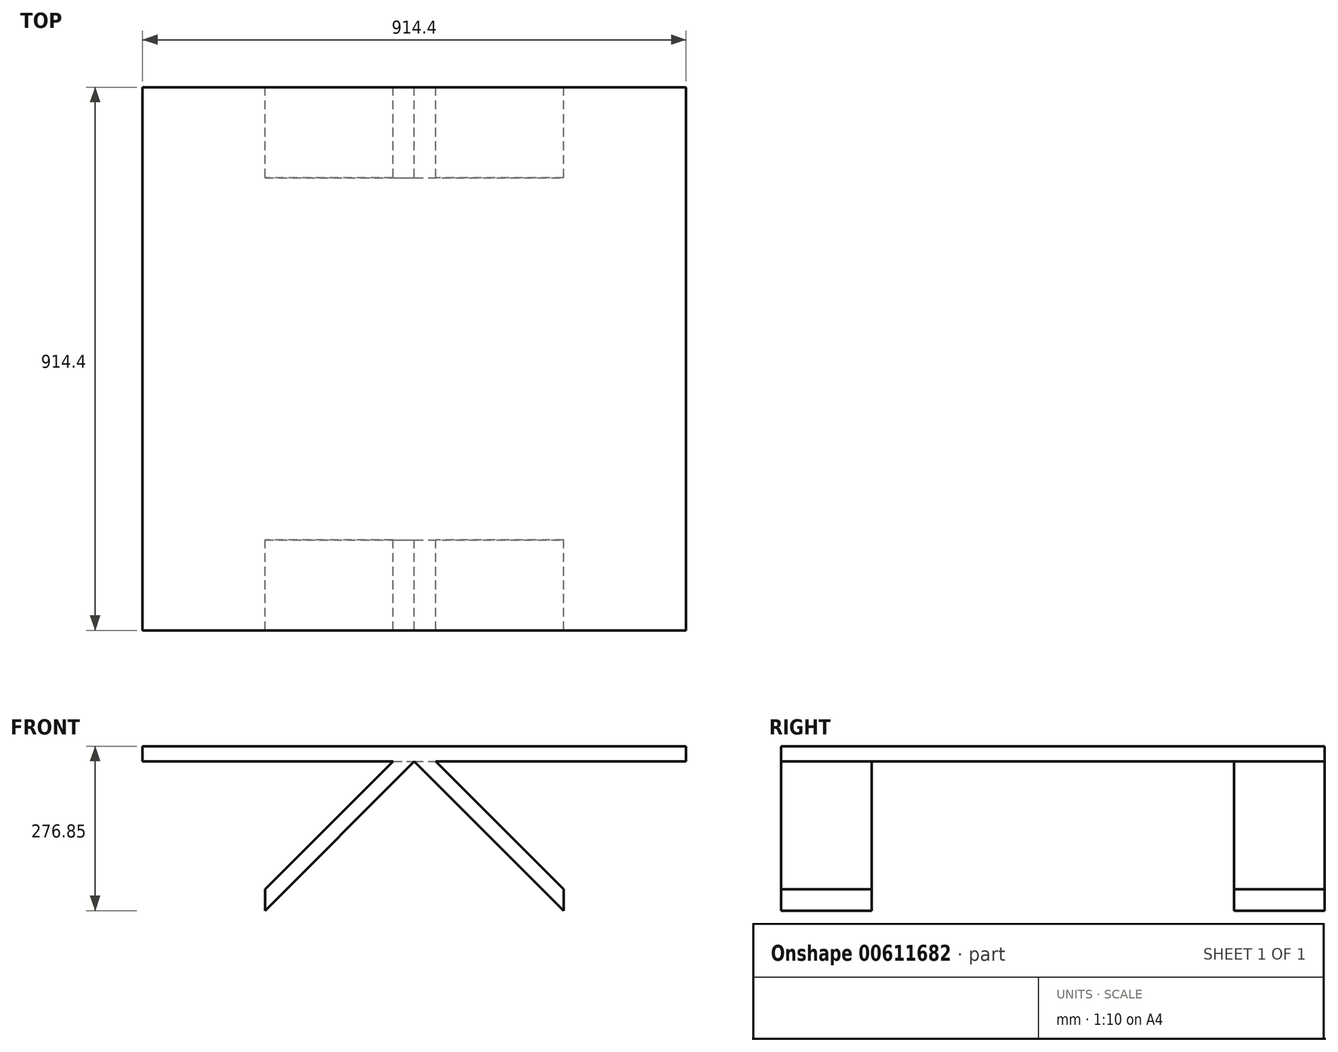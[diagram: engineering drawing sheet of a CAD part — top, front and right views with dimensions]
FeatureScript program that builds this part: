
annotation { "Feature Type Name" : "Feature", "Feature Type Description" : "" }
export const myFeature = defineFeature(function(context is Context, id is Id, definition is map)
    precondition{}
    {
        {
            var Q0;
            Q0=qCreatedBy(makeId("Front.planeOp"),FACE);
            var sketch = newSketch(context, id + "F0", { "sketchPlane" : qUnion([Q0])});
            skLineSegment(sketch, "E0", {"start": v(457.2, 0) * mm, "end": v(-457.2, 0) * mm});
            skLineSegment(sketch, "E1", {"start": v(-457.2, 0) * mm, "end": v(-457.2, 25.4) * mm});
            skLineSegment(sketch, "E2", {"start": v(-457.2, 25.4) * mm, "end": v(457.2, 25.4) * mm});
            skLineSegment(sketch, "E3", {"start": v(457.2, 25.4) * mm, "end": v(457.2, 0) * mm});
            skSolve(sketch);
        }
        {
            var Q0;
            Q0=qCreatedBy(makeId("Front.planeOp"),FACE);
            var sketch = newSketch(context, id + "F1", { "sketchPlane" : qUnion([Q0])});
            skLineSegment(sketch, "E4", {"start": v(-35.92, 0) * mm, "end": v(-251.45, -215.53) * mm});
            skLineSegment(sketch, "E5", {"start": v(-251.45, -215.53) * mm, "end": v(-251.45, -251.45) * mm});
            skLineSegment(sketch, "E6", {"start": v(-251.45, -251.45) * mm, "end": v(0, 0) * mm});
            skLineSegment(sketch, "E7", {"start": v(0, 0) * mm, "end": v(251.45, -251.45) * mm});
            skLineSegment(sketch, "E8", {"start": v(251.45, -251.45) * mm, "end": v(251.45, -215.53) * mm});
            skLineSegment(sketch, "E9", {"start": v(251.45, -215.53) * mm, "end": v(35.92, 0) * mm});
            skPoint(sketch, "E10.start.orphan", {"position": v(-150.22, 0) * mm});
            skPoint(sketch, "E11.end.orphan", {"position": v(152.4, 0) * mm});
            skPoint(sketch, "E11.start.orphan", {"position": v(150.22, -25.4) * mm});
            skLineSegment(sketch, "E12", {"start": v(-35.92, 0) * mm, "end": v(35.92, 0) * mm});
            skSolve(sketch);
        }
        {
            var Q0;
            Q0=makeQuery(id+"F0.imprint","IMPRINT",FACE,{"disambiguationData":[TD([[makeQuery(id+"F0.imprint","IMPRINT",EDGE,{"derivedFrom":sQuery(id+"F0.wireOp",EDGE,"E0")}),-1.0]])]});
            extrude(context, id + "F2", {"entities" : qUnion([Q0]), "endBound" : BoundingType.SYMMETRIC, "depth" : 914.4 * mm, "offsetDistance" : 25.4 * mm});
        }
        {
            var Q0;
            {var subQ0=sQuery(id+"F1.wireOp",EDGE,"E4");Q0=makeQuery(id+"F1.imprint","IMPRINT",FACE,{"disambiguationData":[TD([[makeQuery(id+"F1.imprint","IMPRINT",EDGE,{"derivedFrom":subQ0}),1.0]])]});}
            var Q1;
            {var subQ0=sQuery(id+"F1.wireOp",EDGE,"E7");Q1=makeQuery(id+"F1.imprint","IMPRINT",FACE,{"disambiguationData":[TD([[makeQuery(id+"F1.imprint","IMPRINT",EDGE,{"derivedFrom":subQ0}),1.0]])]});}
            extrude(context, id + "F3", {"entities" : qUnion([Q0, Q1]), "operationType" : NewBodyOperationType.ADD, "endBound" : BoundingType.SYMMETRIC, "depth" : 914.4 * mm, "offsetDistance" : 25.4 * mm});
        }
        {
            var Q0;
            Q0=qCreatedBy(makeId("Front.planeOp"),FACE);
            var sketch = newSketch(context, id + "F4", { "sketchPlane" : qUnion([Q0])});
            skLineSegment(sketch, "E13", {"start": v(-35.92, 0) * mm, "end": v(-251.45, -215.53) * mm});
            skLineSegment(sketch, "E14", {"start": v(-251.45, -215.53) * mm, "end": v(-251.45, -251.45) * mm});
            skLineSegment(sketch, "E15", {"start": v(-251.45, -251.45) * mm, "end": v(0, 0) * mm});
            skLineSegment(sketch, "E16", {"start": v(0, 0) * mm, "end": v(251.45, -251.45) * mm});
            skLineSegment(sketch, "E17", {"start": v(251.45, -251.45) * mm, "end": v(251.45, -215.53) * mm});
            skLineSegment(sketch, "E18", {"start": v(251.45, -215.53) * mm, "end": v(35.92, 0) * mm});
            skPoint(sketch, "E19.start.orphan", {"position": v(-150.22, 0) * mm});
            skPoint(sketch, "E20.end.orphan", {"position": v(153.08, 4.12) * mm});
            skPoint(sketch, "E20.start.orphan", {"position": v(150.22, -21.28) * mm});
            skLineSegment(sketch, "E21", {"start": v(-35.92, 0) * mm, "end": v(35.92, 0) * mm});
            skSolve(sketch);
        }
        {
            var Q0;
            Q0 = qSketchRegion(id + "F4", true);
            extrude(context, id + "F5", {"entities" : qUnion([Q0]), "operationType" : NewBodyOperationType.REMOVE, "endBound" : BoundingType.SYMMETRIC, "depth" : 609.6 * mm, "offsetDistance" : 25.4 * mm});
        }
    });
